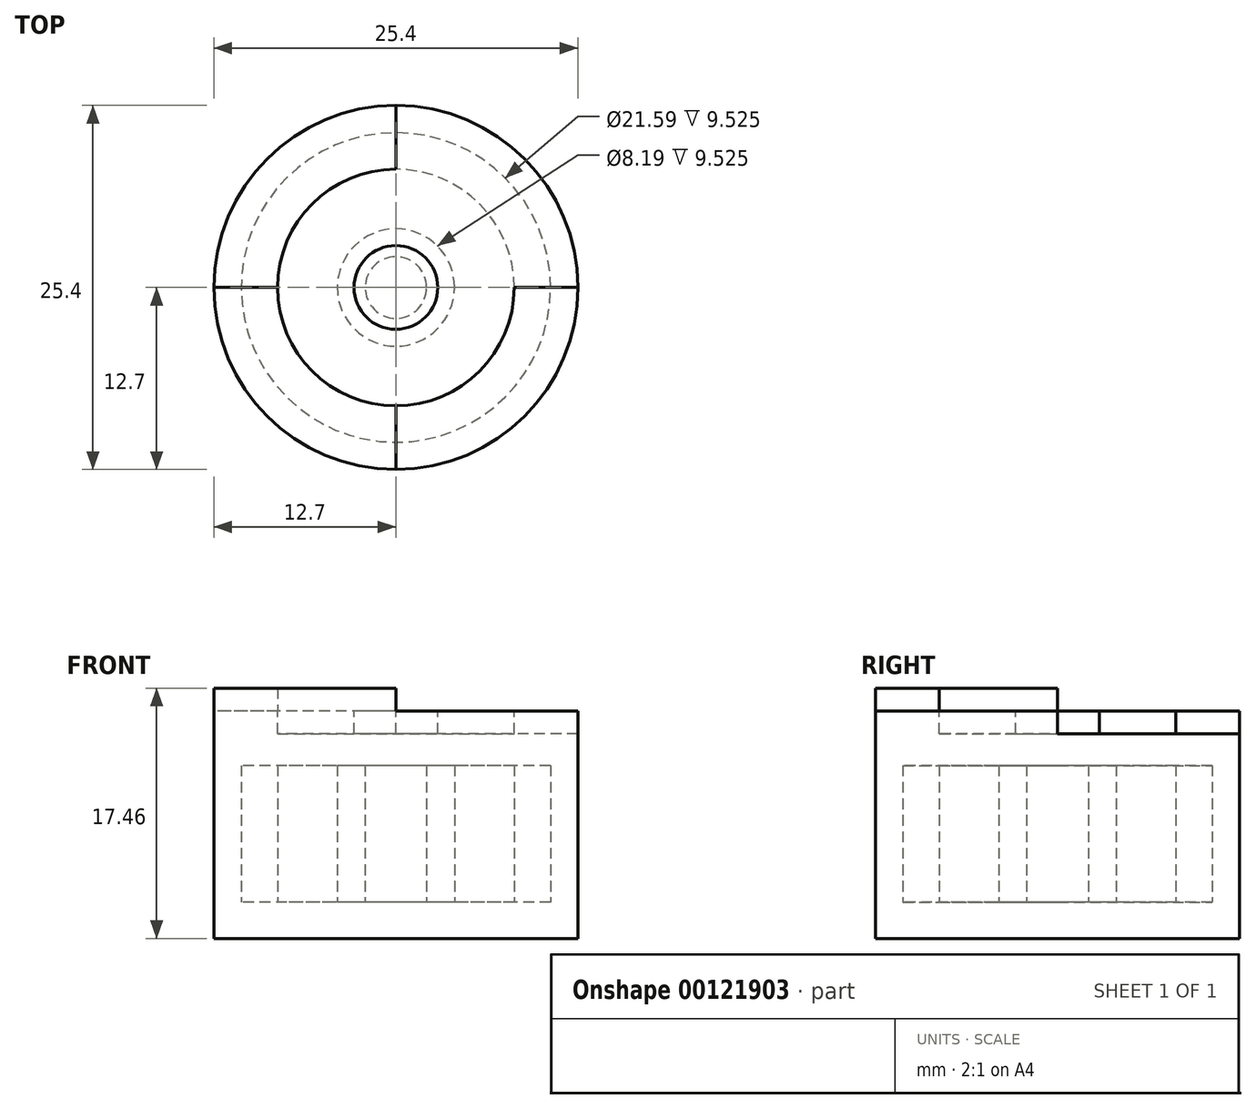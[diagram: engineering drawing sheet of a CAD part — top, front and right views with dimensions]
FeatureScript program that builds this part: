
annotation { "Feature Type Name" : "Feature", "Feature Type Description" : "" }
export const myFeature = defineFeature(function(context is Context, id is Id, definition is map)
    precondition{}
    {
        {
            var Q0;
            Q0=qCreatedBy(makeId("Top.planeOp"),FACE);
            var sketch = newSketch(context, id + "F0", { "sketchPlane" : qUnion([Q0])});
            skCircle(sketch, "E0", {"center": v(0, 0) * mm, "radius": 8.26 * mm});
            skCircle(sketch, "E1", {"center": v(0, 0) * mm, "radius": 2.92 * mm});
            skCircle(sketch, "E2", {"center": v(0, 0) * mm, "radius": 12.7 * mm});
            skSolve(sketch);
        }
        {
            var Q0;
            Q0 = qSketchRegion(id + "F0", true);
            var Q1;
            Q1=makeQuery(id+"F0.imprint","IMPRINT",FACE,{"disambiguationData":[TD([[makeQuery(id+"F0.imprint","IMPRINT",EDGE,{"derivedFrom":sQuery(id+"F0.wireOp",EDGE,"E0")}),1.0]])]});
            var Q2;
            Q2=makeQuery(id+"F0.imprint","IMPRINT",FACE,{"disambiguationData":[TD([[makeQuery(id+"F0.imprint","IMPRINT",EDGE,{"derivedFrom":sQuery(id+"F0.wireOp",EDGE,"E1")}),1.0]])]});
            extrude(context, id + "F1", {"entities" : qUnion([Q0, Q1, Q2]), "depth" : 15.88 * mm});
        }
        {
            var Q0;
            Q0=makeQuery(id+"F1.opExtrude","CAP_FACE",FACE,{"disambiguationData":[OSD([sQuery(id+"F0.wireOp",EDGE,"E2")])],"isStart":false});
            var sketch = newSketch(context, id + "F2", { "sketchPlane" : qUnion([Q0])});
            skCircle(sketch, "E3.0", {"center": v(0, 0) * mm, "radius": 8.26 * mm});
            skCircle(sketch, "E4.0", {"center": v(0, 0) * mm, "radius": 2.92 * mm});
            skSolve(sketch);
        }
        {
            var Q0;
            Q0 = qSketchRegion(id + "F2", true);
            extrude(context, id + "F3", {"entities" : qUnion([Q0]), "operationType" : NewBodyOperationType.REMOVE, "oppositeDirection" : true, "depth" : 1.59 * mm});
        }
        {
            var Q0;
            {var subQ0=sQuery(id+"F0.wireOp",EDGE,"E2");Q0=makeQuery(id+"F3.boolean.opBoolean","SPLIT",FACE,{"disambiguationData":[TD([makeQuery(id+"F1.opExtrude","SWEPT_FACE",FACE,{"disambiguationData":[OSD([subQ0])]})])],"derivedFrom":makeQuery(id+"F1.opExtrude","CAP_FACE",FACE,{"disambiguationData":[OSD([subQ0])],"isStart":false})});}
            var sketch = newSketch(context, id + "F4", { "sketchPlane" : qUnion([Q0])});
            skCircle(sketch, "E5.0", {"center": v(0, 0) * mm, "radius": 8.26 * mm});
            skCircle(sketch, "E5.1", {"center": v(0, 0) * mm, "radius": 12.7 * mm});
            skLineSegment(sketch, "E6.bottom", {"start": v(0, 0) * mm, "end": v(18, 0) * mm});
            skLineSegment(sketch, "E6.top", {"start": v(0, 16.15) * mm, "end": v(18, 16.15) * mm});
            skLineSegment(sketch, "E6.left", {"start": v(0, 0) * mm, "end": v(0, 16.15) * mm});
            skLineSegment(sketch, "E6.right", {"start": v(18, 0) * mm, "end": v(18, 16.15) * mm});
            skLineSegment(sketch, "E7.bottom", {"start": v(0, 0) * mm, "end": v(-14.74, 0) * mm});
            skLineSegment(sketch, "E7.top", {"start": v(0, -16.25) * mm, "end": v(-14.74, -16.25) * mm});
            skLineSegment(sketch, "E7.left", {"start": v(0, 0) * mm, "end": v(0, -16.25) * mm});
            skLineSegment(sketch, "E7.right", {"start": v(-14.74, 0) * mm, "end": v(-14.74, -16.25) * mm});
            skSolve(sketch);
        }
        {
            var Q0;
            {var subQ0=sQuery(id+"F4.wireOp",EDGE,"E6.bottom");var subQ1=sQuery(id+"F4.wireOp",EDGE,"E5.0");var subQ2=makeQuery(id+"F4.imprint","INTERSECT",VERTEX,{"derivedFrom":[subQ1,subQ0]});Q0=makeQuery(id+"F4.imprint","IMPRINT",FACE,{"disambiguationData":[TD([[makeQuery(id+"F4.imprint","IMPRINT",EDGE,{"disambiguationData":[TD([[subQ2,-1.0]])],"derivedFrom":subQ1}),-1.0]])]});}
            var Q1;
            Q1=makeQuery(id+"F3.boolean.opBoolean","COPY",FACE,{"derivedFrom":makeQuery(id+"F3.opExtrude","CAP_FACE",FACE,{"disambiguationData":[OSD([sQuery(id+"F2.wireOp",EDGE,"E3.0"),sQuery(id+"F2.wireOp",EDGE,"E4.0")])],"isStart":false})});
            extrude(context, id + "F5", {"entities" : qUnion([Q0]), "operationType" : NewBodyOperationType.REMOVE, "endBound" : BoundingType.UP_TO_SURFACE, "oppositeDirection" : true, "endBoundEntityFace" : qUnion([Q1]), "depth" : 25.4 * mm});
        }
        {
            var Q0;
            {var subQ0=sQuery(id+"F0.wireOp",EDGE,"E2");Q0=makeQuery(id+"F3.boolean.opBoolean","SPLIT",FACE,{"disambiguationData":[TD([makeQuery(id+"F1.opExtrude","SWEPT_FACE",FACE,{"disambiguationData":[OSD([subQ0])]})])],"derivedFrom":makeQuery(id+"F1.opExtrude","CAP_FACE",FACE,{"disambiguationData":[OSD([subQ0])],"isStart":false})});}
            var sketch = newSketch(context, id + "F6", { "sketchPlane" : qUnion([Q0])});
            skArc(sketch, "E8.0.0", {"start": v(0, -8.26) * mm, "mid": v(-5.84, -5.84) * mm, "end": v(-8.26, 0) * mm});
            skLineSegment(sketch, "E8.0.1", {"start": v(-8.26, 0) * mm, "end": v(-12.7, 0) * mm});
            skArc(sketch, "E8.0.2", {"start": v(-12.7, 0) * mm, "mid": v(-8.98, -8.98) * mm, "end": v(0, -12.7) * mm});
            skLineSegment(sketch, "E8.0.3", {"start": v(0, -12.7) * mm, "end": v(0, -8.26) * mm});
            skSolve(sketch);
        }
        {
            var Q0;
            Q0 = qSketchRegion(id + "F6", true);
            extrude(context, id + "F7", {"entities" : qUnion([Q0]), "operationType" : NewBodyOperationType.ADD, "depth" : 1.59 * mm});
        }
        {
            var Q0;
            Q0=makeQuery(id+"F0.imprint","IMPRINT",FACE,{"disambiguationData":[TD([[makeQuery(id+"F0.imprint","IMPRINT",EDGE,{"derivedFrom":sQuery(id+"F0.wireOp",EDGE,"E0")}),-1.0]])]});
            cPlane(context, id + "F8", {"entities" : qUnion([Q0]), "cplaneType" : CPlaneType.OFFSET, "offset" : 2.54 * mm, "width" : 152.4 * mm, "height" : 152.4 * mm});
        }
        {
            var Q0;
            Q0=qCreatedBy(id+"F8.planeOp",FACE);
            var sketch = newSketch(context, id + "F9", { "sketchPlane" : qUnion([Q0])});
            skCircle(sketch, "E9.0", {"center": v(0, 0) * mm, "radius": 8.26 * mm});
            skCircle(sketch, "E10.0", {"center": v(0, 0) * mm, "radius": 10.8 * mm});
            skSolve(sketch);
        }
        {
            var Q0;
            Q0 = qSketchRegion(id + "F9", true);
            extrude(context, id + "F10", {"entities" : qUnion([Q0]), "operationType" : NewBodyOperationType.REMOVE, "depth" : 9.52 * mm});
        }
        {
            var Q0;
            Q0=qCreatedBy(id+"F8.planeOp",FACE);
            var sketch = newSketch(context, id + "F11", { "sketchPlane" : qUnion([Q0])});
            skCircle(sketch, "E11.0", {"center": v(0, 0) * mm, "radius": 4.1 * mm});
            skCircle(sketch, "E12", {"center": v(0, 0) * mm, "radius": 2.15 * mm});
            skSolve(sketch);
        }
        {
            var Q0;
            Q0 = qSketchRegion(id + "F11", true);
            extrude(context, id + "F12", {"entities" : qUnion([Q0]), "operationType" : NewBodyOperationType.REMOVE, "depth" : 9.52 * mm});
        }
    });
